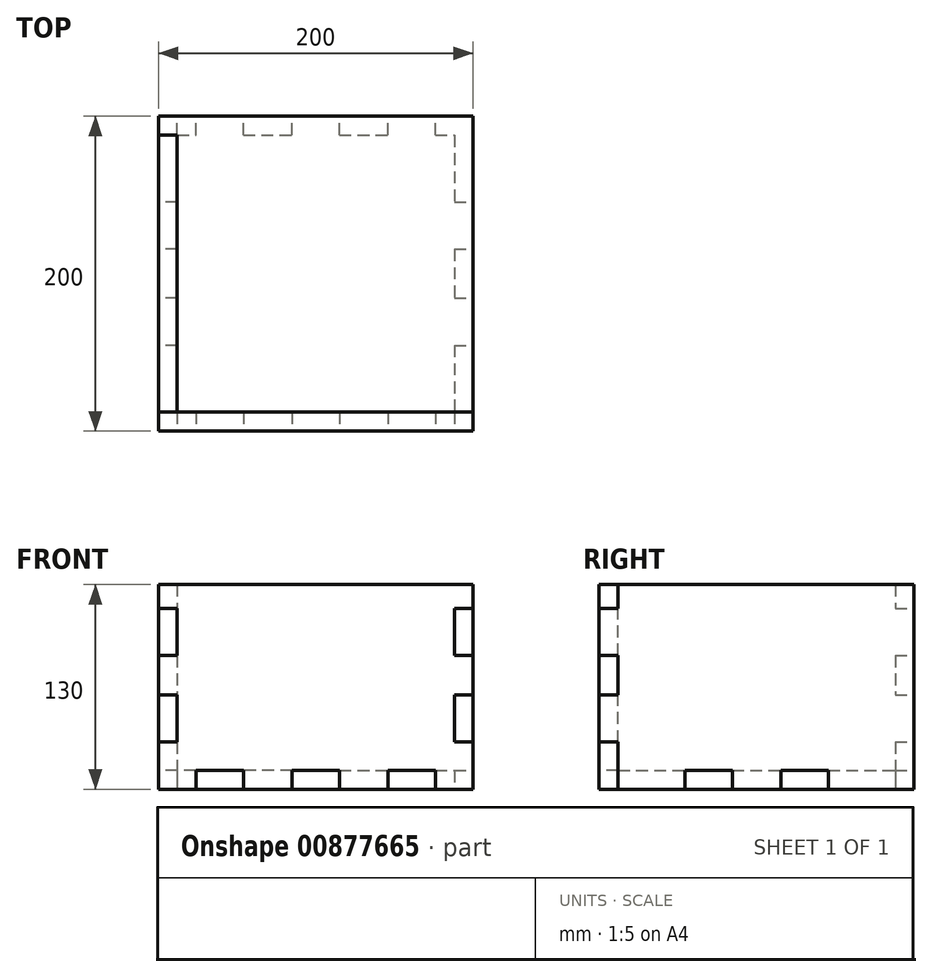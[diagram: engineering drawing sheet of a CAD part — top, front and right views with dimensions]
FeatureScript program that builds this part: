
annotation { "Feature Type Name" : "Feature", "Feature Type Description" : "" }
export const myFeature = defineFeature(function(context is Context, id is Id, definition is map)
    precondition{}
    {
        {
            var Q0;
            Q0=qCreatedBy(makeId("Top.planeOp"),FACE);
            var sketch = newSketch(context, id + "F0", { "sketchPlane" : qUnion([Q0])});
            skLineSegment(sketch, "E0.bottom", {"start": v(100, 100) * mm, "end": v(-100, 100) * mm});
            skLineSegment(sketch, "E0.top", {"start": v(100, -100) * mm, "end": v(-100, -100) * mm});
            skLineSegment(sketch, "E0.left", {"start": v(100, 100) * mm, "end": v(100, -100) * mm});
            skLineSegment(sketch, "E0.right", {"start": v(-100, 100) * mm, "end": v(-100, -100) * mm});
            skPoint(sketch, "E0.middle", {"position": v(0, 0) * mm});
            skLineSegment(sketch, "E1.bottom", {"start": v(-75.93, 27.2) * mm, "end": v(-14.12, 27.2) * mm});
            skLineSegment(sketch, "E1.top", {"start": v(-75.93, -21.09) * mm, "end": v(-14.12, -21.09) * mm});
            skLineSegment(sketch, "E1.left", {"start": v(-75.93, 27.2) * mm, "end": v(-75.93, -21.09) * mm});
            skLineSegment(sketch, "E1.right", {"start": v(-14.12, 27.2) * mm, "end": v(-14.12, -21.09) * mm});
            skSolve(sketch);
        }
        {
            var Q0;
            Q0=makeQuery(id+"F0.imprint","IMPRINT",FACE,{"disambiguationData":[TD([[makeQuery(id+"F0.imprint","IMPRINT",EDGE,{"derivedFrom":sQuery(id+"F0.wireOp",EDGE,"E0.bottom")}),1.0]])]});
            var Q1;
            Q1=makeQuery(id+"F0.imprint","IMPRINT",FACE,{"disambiguationData":[TD([[makeQuery(id+"F0.imprint","IMPRINT",EDGE,{"derivedFrom":sQuery(id+"F0.wireOp",EDGE,"E1.bottom")}),-1.0]])]});
            extrude(context, id + "F1", {"entities" : qUnion([Q0, Q1]), "depth" : 130 * mm, "offsetDistance" : 25 * mm});
        }
        {
            var Q0;
            Q0=makeQuery(id+"F1.opExtrude","CAP_FACE",FACE,{"disambiguationData":[OSD([sQuery(id+"F0.wireOp",EDGE,"E0.bottom"),sQuery(id+"F0.wireOp",EDGE,"E0.top"),sQuery(id+"F0.wireOp",EDGE,"E0.left"),sQuery(id+"F0.wireOp",EDGE,"E0.right")])],"isStart":true});
            var sketch = newSketch(context, id + "F2", { "sketchPlane" : qUnion([Q0])});
            skLineSegment(sketch, "E2.0", {"start": v(88, 88) * mm, "end": v(76, 88) * mm});
            skLineSegment(sketch, "E2.1", {"start": v(88, -88) * mm, "end": v(88, -45.5) * mm});
            skLineSegment(sketch, "E2.2", {"start": v(-88, -88) * mm, "end": v(-76, -88) * mm});
            skLineSegment(sketch, "E2.3", {"start": v(-88, 88) * mm, "end": v(-88, 45.5) * mm});
            skLineSegment(sketch, "E3.top", {"start": v(-76, 100) * mm, "end": v(-46, 100) * mm});
            skLineSegment(sketch, "E3.left", {"start": v(-76, 88) * mm, "end": v(-76, 100) * mm});
            skLineSegment(sketch, "E3.right", {"start": v(-46, 88) * mm, "end": v(-46, 100) * mm});
            skLineSegment(sketch, "E4.top", {"start": v(-15, 100) * mm, "end": v(15, 100) * mm});
            skLineSegment(sketch, "E4.left", {"start": v(-15, 88) * mm, "end": v(-15, 100) * mm});
            skLineSegment(sketch, "E4.right", {"start": v(15, 88) * mm, "end": v(15, 100) * mm});
            skLineSegment(sketch, "E5", {"start": v(0, 0) * mm, "end": v(0, 100) * mm, "construction": true});
            skLineSegment(sketch, "E6.trimOffspring", {"start": v(-76, 88) * mm, "end": v(-88, 88) * mm});
            skLineSegment(sketch, "E7.trimOffspring", {"start": v(-15, 88) * mm, "end": v(-46, 88) * mm});
            skLineSegment(sketch, "E8.MirrorCS", {"start": v(46, 88) * mm, "end": v(46, 100) * mm});
            skLineSegment(sketch, "E9.MirrorCS", {"start": v(76, 100) * mm, "end": v(46, 100) * mm});
            skLineSegment(sketch, "E10.MirrorCS", {"start": v(76, 88) * mm, "end": v(76, 100) * mm});
            skLineSegment(sketch, "E11.trimOffspring", {"start": v(46, 88) * mm, "end": v(15, 88) * mm});
            skLineSegment(sketch, "E12", {"start": v(0, 0) * mm, "end": v(88, 0) * mm, "construction": true});
            skLineSegment(sketch, "E13.MirrorCS", {"start": v(-76, -88) * mm, "end": v(-76, -100) * mm});
            skLineSegment(sketch, "E14.MirrorCS", {"start": v(-76, -100) * mm, "end": v(-46, -100) * mm});
            skLineSegment(sketch, "E15.MirrorCS", {"start": v(-46, -88) * mm, "end": v(-46, -100) * mm});
            skLineSegment(sketch, "E16.MirrorCS", {"start": v(-15, -88) * mm, "end": v(-15, -100) * mm});
            skLineSegment(sketch, "E17.MirrorCS", {"start": v(-15, -100) * mm, "end": v(15, -100) * mm});
            skLineSegment(sketch, "E18.MirrorCS", {"start": v(15, -88) * mm, "end": v(15, -100) * mm});
            skLineSegment(sketch, "E19.MirrorCS", {"start": v(46, -88) * mm, "end": v(46, -100) * mm});
            skLineSegment(sketch, "E20.MirrorCS", {"start": v(76, -100) * mm, "end": v(46, -100) * mm});
            skLineSegment(sketch, "E21.MirrorCS", {"start": v(76, -88) * mm, "end": v(76, -100) * mm});
            skLineSegment(sketch, "E22.trimOffspring", {"start": v(-46, -88) * mm, "end": v(-15, -88) * mm});
            skLineSegment(sketch, "E23.trimOffspring", {"start": v(15, -88) * mm, "end": v(46, -88) * mm});
            skLineSegment(sketch, "E24.trimOffspring", {"start": v(76, -88) * mm, "end": v(88, -88) * mm});
            skLineSegment(sketch, "E25.bottom", {"start": v(-88, 15.5) * mm, "end": v(-100, 15.5) * mm});
            skLineSegment(sketch, "E25.top", {"start": v(-88, 45.5) * mm, "end": v(-100, 45.5) * mm});
            skLineSegment(sketch, "E25.right", {"start": v(-100, 15.5) * mm, "end": v(-100, 45.5) * mm});
            skLineSegment(sketch, "E26.MirrorCS", {"start": v(-88, -15.5) * mm, "end": v(-100, -15.5) * mm});
            skLineSegment(sketch, "E27.MirrorCS", {"start": v(-100, -15.5) * mm, "end": v(-100, -45.5) * mm});
            skLineSegment(sketch, "E28.MirrorCS", {"start": v(-88, -45.5) * mm, "end": v(-100, -45.5) * mm});
            skLineSegment(sketch, "E29.MirrorCS", {"start": v(88, 45.5) * mm, "end": v(100, 45.5) * mm});
            skLineSegment(sketch, "E30.MirrorCS", {"start": v(100, 15.5) * mm, "end": v(100, 45.5) * mm});
            skLineSegment(sketch, "E31.MirrorCS", {"start": v(88, 15.5) * mm, "end": v(100, 15.5) * mm});
            skLineSegment(sketch, "E32.MirrorCS", {"start": v(88, -15.5) * mm, "end": v(100, -15.5) * mm});
            skLineSegment(sketch, "E33.MirrorCS", {"start": v(100, -15.5) * mm, "end": v(100, -45.5) * mm});
            skLineSegment(sketch, "E34.MirrorCS", {"start": v(88, -45.5) * mm, "end": v(100, -45.5) * mm});
            skLineSegment(sketch, "E35.trimOffspring", {"start": v(-88, 15.5) * mm, "end": v(-88, -15.5) * mm});
            skLineSegment(sketch, "E36.trimOffspring", {"start": v(-88, -45.5) * mm, "end": v(-88, -88) * mm});
            skLineSegment(sketch, "E37.trimOffspring", {"start": v(88, -15.5) * mm, "end": v(88, 15.5) * mm});
            skLineSegment(sketch, "E38.trimOffspring", {"start": v(88, 45.5) * mm, "end": v(88, 88) * mm});
            skSolve(sketch);
        }
        {
            var Q0;
            Q0 = qSketchRegion(id + "F2", true);
            extrude(context, id + "F3", {"entities" : qUnion([Q0]), "oppositeDirection" : true, "depth" : 12 * mm, "offsetDistance" : 25 * mm});
        }
        {
            var Q0;
            Q0=makeQuery(id+"F1.opExtrude","SWEPT_FACE",FACE,{"disambiguationData":[OSD([sQuery(id+"F0.wireOp",EDGE,"E0.top")])]});
            var sketch = newSketch(context, id + "F4", { "sketchPlane" : qUnion([Q0])});
            skLineSegment(sketch, "E39.0", {"start": v(-76, 12) * mm, "end": v(-76, 0) * mm});
            skLineSegment(sketch, "E40.0", {"start": v(-46, 12) * mm, "end": v(-76, 12) * mm});
            skLineSegment(sketch, "E41.0", {"start": v(-46, 12) * mm, "end": v(-46, 0) * mm});
            skLineSegment(sketch, "E42.0", {"start": v(-15, 12) * mm, "end": v(-15, 0) * mm});
            skLineSegment(sketch, "E43.0", {"start": v(15, 12) * mm, "end": v(-15, 12) * mm});
            skLineSegment(sketch, "E44.0", {"start": v(15, 12) * mm, "end": v(15, 0) * mm});
            skLineSegment(sketch, "E45.0", {"start": v(46, 12) * mm, "end": v(46, 0) * mm});
            skLineSegment(sketch, "E46.0", {"start": v(76, 12) * mm, "end": v(46, 12) * mm});
            skLineSegment(sketch, "E47.0", {"start": v(76, 12) * mm, "end": v(76, 0) * mm});
            skLineSegment(sketch, "E48.0", {"start": v(100, 0) * mm, "end": v(76, 0) * mm});
            skLineSegment(sketch, "E49.0", {"start": v(-100, 130) * mm, "end": v(-100, 115) * mm});
            skLineSegment(sketch, "E50.0", {"start": v(100, 130) * mm, "end": v(-100, 130) * mm});
            skLineSegment(sketch, "E51.0", {"start": v(100, 130) * mm, "end": v(100, 115) * mm});
            skLineSegment(sketch, "E52.trimOffspring", {"start": v(-76, 0) * mm, "end": v(-100, 0) * mm});
            skLineSegment(sketch, "E53.trimOffspring", {"start": v(-15, 0) * mm, "end": v(-46, 0) * mm});
            skLineSegment(sketch, "E54.trimOffspring", {"start": v(46, 0) * mm, "end": v(15, 0) * mm});
            skLineSegment(sketch, "E55.bottom", {"start": v(100, 30) * mm, "end": v(88, 30) * mm});
            skLineSegment(sketch, "E55.top", {"start": v(100, 60) * mm, "end": v(88, 60) * mm});
            skLineSegment(sketch, "E55.right", {"start": v(88, 30) * mm, "end": v(88, 60) * mm});
            skLineSegment(sketch, "E56.bottom", {"start": v(100, 85) * mm, "end": v(88, 85) * mm});
            skLineSegment(sketch, "E56.top", {"start": v(100, 115) * mm, "end": v(88, 115) * mm});
            skLineSegment(sketch, "E56.right", {"start": v(88, 85) * mm, "end": v(88, 115) * mm});
            skLineSegment(sketch, "E57", {"start": v(0, 130) * mm, "end": v(0, 60.9) * mm, "construction": true});
            skLineSegment(sketch, "E58.MirrorCS", {"start": v(-100, 115) * mm, "end": v(-88, 115) * mm});
            skLineSegment(sketch, "E59.MirrorCS", {"start": v(-88, 85) * mm, "end": v(-88, 115) * mm});
            skLineSegment(sketch, "E60.MirrorCS", {"start": v(-100, 85) * mm, "end": v(-88, 85) * mm});
            skLineSegment(sketch, "E61.MirrorCS", {"start": v(-100, 60) * mm, "end": v(-88, 60) * mm});
            skLineSegment(sketch, "E62.MirrorCS", {"start": v(-88, 30) * mm, "end": v(-88, 60) * mm});
            skLineSegment(sketch, "E63.MirrorCS", {"start": v(-100, 30) * mm, "end": v(-88, 30) * mm});
            skLineSegment(sketch, "E64.trimOffspring", {"start": v(100, 85) * mm, "end": v(100, 60) * mm});
            skLineSegment(sketch, "E65.trimOffspring", {"start": v(100, 30) * mm, "end": v(100, 0) * mm});
            skLineSegment(sketch, "E66.trimOffspring", {"start": v(-100, 30) * mm, "end": v(-100, 0) * mm});
            skLineSegment(sketch, "E67.trimOffspring", {"start": v(-100, 85) * mm, "end": v(-100, 60) * mm});
            skSolve(sketch);
        }
        {
            var Q0;
            Q0 = qSketchRegion(id + "F4", true);
            extrude(context, id + "F5", {"entities" : qUnion([Q0]), "oppositeDirection" : true, "depth" : 12 * mm, "offsetDistance" : 25 * mm});
        }
        {
            var Q0;
            Q0=makeQuery(id+"F1.opExtrude","SWEPT_FACE",FACE,{"disambiguationData":[OSD([sQuery(id+"F0.wireOp",EDGE,"E0.right")])]});
            var sketch = newSketch(context, id + "F6", { "sketchPlane" : qUnion([Q0])});
            skLineSegment(sketch, "E68", {"start": v(0, 130) * mm, "end": v(0, 0) * mm});
            skLineSegment(sketch, "E69.0", {"start": v(15.5, 12) * mm, "end": v(15.5, 0) * mm});
            skLineSegment(sketch, "E70.0", {"start": v(15.5, 12) * mm, "end": v(45.5, 12) * mm});
            skLineSegment(sketch, "E71.0", {"start": v(45.5, 12) * mm, "end": v(45.5, 0) * mm});
            skLineSegment(sketch, "E72.0", {"start": v(88, 30) * mm, "end": v(88, 0) * mm});
            skLineSegment(sketch, "E73.0", {"start": v(0, 0) * mm, "end": v(15.5, 0) * mm});
            skLineSegment(sketch, "E74.0", {"start": v(100, 115) * mm, "end": v(100, 85) * mm});
            skLineSegment(sketch, "E75.0", {"start": v(88, 60) * mm, "end": v(100, 60) * mm});
            skLineSegment(sketch, "E76.0", {"start": v(88, 85) * mm, "end": v(88, 60) * mm});
            skPoint(sketch, "E77.0", {"position": v(94, 85) * mm});
            skLineSegment(sketch, "E78.0", {"start": v(88, 85) * mm, "end": v(100, 85) * mm});
            skLineSegment(sketch, "E79.0", {"start": v(88, 115) * mm, "end": v(100, 115) * mm});
            skLineSegment(sketch, "E80.0", {"start": v(88, 130) * mm, "end": v(88, 115) * mm});
            skLineSegment(sketch, "E81.0", {"start": v(0, 130) * mm, "end": v(88, 130) * mm});
            skPoint(sketch, "E82.orphan", {"position": v(-100, 130) * mm});
            skPoint(sketch, "E83.orphan", {"position": v(-100, 0) * mm});
            skLineSegment(sketch, "E84.trimOffspring", {"start": v(45.5, 0) * mm, "end": v(88, 0) * mm});
            skLineSegment(sketch, "E85.0", {"start": v(88, 30) * mm, "end": v(100, 30) * mm});
            skPoint(sketch, "E86.orphan", {"position": v(100, 0) * mm});
            skLineSegment(sketch, "E87.trimOffspring", {"start": v(100, 60) * mm, "end": v(100, 30) * mm});
            skPoint(sketch, "E88.orphan", {"position": v(100, 130) * mm});
            skLineSegment(sketch, "E89.MirrorCS", {"start": v(-88, 85) * mm, "end": v(-100, 85) * mm});
            skLineSegment(sketch, "E90.MirrorCS", {"start": v(-88, 30) * mm, "end": v(-88, 0) * mm});
            skLineSegment(sketch, "E91.MirrorCS", {"start": v(-45.5, 12) * mm, "end": v(-45.5, 0) * mm});
            skLineSegment(sketch, "E92.MirrorCS", {"start": v(-88, 85) * mm, "end": v(-88, 60) * mm});
            skLineSegment(sketch, "E93.MirrorCS", {"start": v(-88, 115) * mm, "end": v(-100, 115) * mm});
            skLineSegment(sketch, "E94.MirrorCS", {"start": v(-88, 130) * mm, "end": v(-88, 115) * mm});
            skLineSegment(sketch, "E95.MirrorCS", {"start": v(0, 130) * mm, "end": v(-88, 130) * mm});
            skLineSegment(sketch, "E96.MirrorCS", {"start": v(-45.5, 0) * mm, "end": v(-88, 0) * mm});
            skLineSegment(sketch, "E97.MirrorCS", {"start": v(-15.5, 12) * mm, "end": v(-45.5, 12) * mm});
            skLineSegment(sketch, "E98.MirrorCS", {"start": v(-88, 60) * mm, "end": v(-100, 60) * mm});
            skPoint(sketch, "E99.MirrorP", {"position": v(-94, 85) * mm});
            skLineSegment(sketch, "E100.MirrorCS", {"start": v(0, 0) * mm, "end": v(-15.5, 0) * mm});
            skLineSegment(sketch, "E101.MirrorCS", {"start": v(-100, 60) * mm, "end": v(-100, 30) * mm});
            skLineSegment(sketch, "E102.MirrorCS", {"start": v(-88, 30) * mm, "end": v(-100, 30) * mm});
            skLineSegment(sketch, "E103.MirrorCS", {"start": v(-100, 115) * mm, "end": v(-100, 85) * mm});
            skLineSegment(sketch, "E104.MirrorCS", {"start": v(-15.5, 12) * mm, "end": v(-15.5, 0) * mm});
            skSolve(sketch);
        }
        {
            var Q0;
            Q0 = qSketchRegion(id + "F6", true);
            extrude(context, id + "F7", {"entities" : qUnion([Q0]), "oppositeDirection" : true, "depth" : 12 * mm, "offsetDistance" : 25 * mm});
        }
    });
